# Revit family: WindowShade_RolleaseAcmeda_ContractSeries1_OpenRoll_R20
name_source: partatom
category: Specialty Equipment
units: mm (PartAtom-declared; Revit-internal decimal feet)

## family parameters
Always vertical = Yes
Cut with Voids When Loaded = No
Host = Wall
Part Type = Normal
Room Calculation Point = No
Round Connector Dimension = Use Diameter
Shared = No

## types (3) — shared parameters
Ceiling Mounted = No
Chain Length = 6' - 9 19/32"
Default Elevation = 10' - 0"
Description = RAC Series 1 - Open Roll
Drop Bar Internal Hem = No
Drop Bar Silent Weight = Yes
Finish = RA - FINISH - WHITE
Input Bracket Width = 5' - 0"
Input Shade Drop = 8' - 0"
Manufacturer = Rollease Acmeda
Model = RA Contract Series
SHADE DROP (DEFAULT) = 8' - 0"
SHADE WIDTH (DEFAULT) = 5' - 0"
Shade = RA - FABRIC - AMBIENT REVIEW
URL = https://www.rolleaseacmedacontract.com
Weight Bar = RA - FINISH - WHITE

## per-type parameters (varying)
| type | Drive Manual LH (Select One) | Drive Manual Left Calc | Drive Manual RH (Select One) | Drive Manual Right Calc | Drive Motorized (Select One) | Drive Motorized Calc |
| 5'W x 8'Drop - Manual Right | No | No | Yes | Yes | No | No |
| 5'W x 8'Drop - Manual Left | Yes | Yes | No | No | No | No |
| 5'W x 8'Drop - Motorized | No | No | No | No | Yes | Yes |

## geometry (parser evidence)
native form markers: Sweep x18
no freeform markers — native parametric forms only
